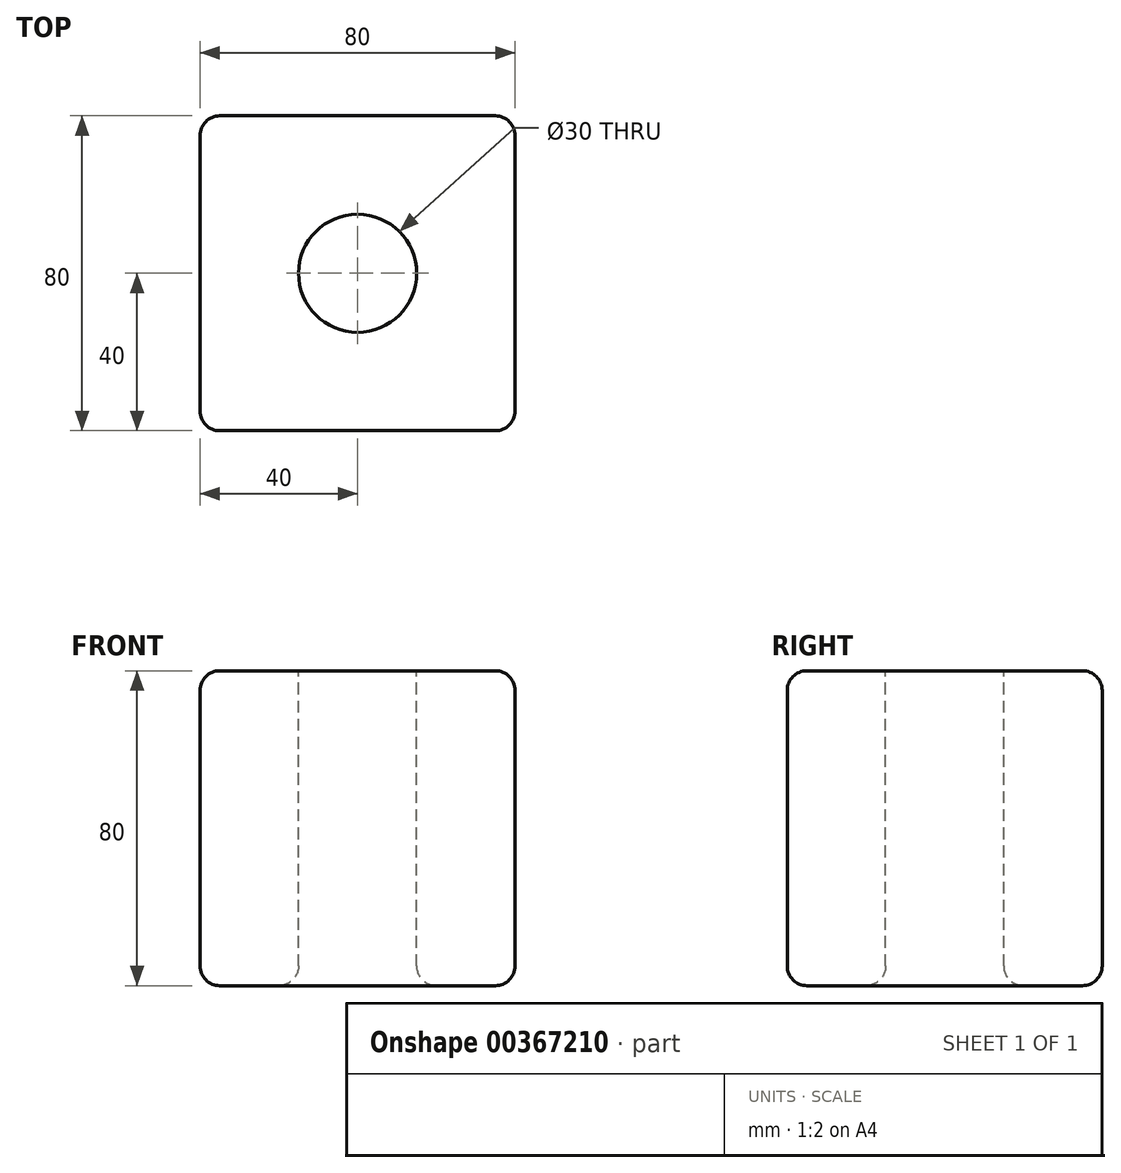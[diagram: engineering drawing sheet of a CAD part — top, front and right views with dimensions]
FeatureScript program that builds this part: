
annotation { "Feature Type Name" : "Feature", "Feature Type Description" : "" }
export const myFeature = defineFeature(function(context is Context, id is Id, definition is map)
    precondition{}
    {
        {
            var Q0;
            Q0=qCreatedBy(makeId("Top.planeOp"),FACE);
            var sketch = newSketch(context, id + "F0", { "sketchPlane" : qUnion([Q0])});
            skLineSegment(sketch, "E0.bottom", {"start": v(40, -40) * mm, "end": v(-40, -40) * mm});
            skLineSegment(sketch, "E0.top", {"start": v(40, 40) * mm, "end": v(-40, 40) * mm});
            skLineSegment(sketch, "E0.left", {"start": v(40, -40) * mm, "end": v(40, 40) * mm});
            skLineSegment(sketch, "E0.right", {"start": v(-40, -40) * mm, "end": v(-40, 40) * mm});
            skPoint(sketch, "E0.middle", {"position": v(0, 0) * mm});
            skSolve(sketch);
        }
        {
            var Q0;
            Q0=makeQuery(id+"F0.imprint","IMPRINT",FACE,{"disambiguationData":[TD([[makeQuery(id+"F0.imprint","IMPRINT",EDGE,{"derivedFrom":sQuery(id+"F0.wireOp",EDGE,"E0.bottom")}),-1.0]])]});
            extrude(context, id + "F1", {"entities" : qUnion([Q0]), "depth" : 80 * mm});
        }
        {
            var Q0;
            Q0=makeQuery(id+"F1.opExtrude","CAP_FACE",FACE,{"disambiguationData":[OSD([sQuery(id+"F0.wireOp",EDGE,"E0.bottom"),sQuery(id+"F0.wireOp",EDGE,"E0.top"),sQuery(id+"F0.wireOp",EDGE,"E0.left"),sQuery(id+"F0.wireOp",EDGE,"E0.right")])],"isStart":false});
            var sketch = newSketch(context, id + "F2", { "sketchPlane" : qUnion([Q0])});
            skCircle(sketch, "E1", {"center": v(0, 0) * mm, "radius": 15 * mm});
            skSolve(sketch);
        }
        {
            var Q0;
            Q0=makeQuery(id+"F2.imprint","IMPRINT",FACE,{"disambiguationData":[TD([[makeQuery(id+"F2.imprint","IMPRINT",EDGE,{"derivedFrom":sQuery(id+"F2.wireOp",EDGE,"E1")}),1.0]])]});
            extrude(context, id + "F3", {"entities" : qUnion([Q0]), "operationType" : NewBodyOperationType.REMOVE, "endBound" : BoundingType.THROUGH_ALL, "oppositeDirection" : true, "depth" : 25 * mm});
        }
        {
            var Q0;
            Q0=makeQuery(id+"F1.opExtrude","CAP_EDGE",EDGE,{"disambiguationData":[OSD([sQuery(id+"F0.wireOp",EDGE,"E0.top")])],"isStart":false});
            var Q1;
            Q1=makeQuery(id+"F1.opExtrude","CAP_EDGE",EDGE,{"disambiguationData":[OSD([sQuery(id+"F0.wireOp",EDGE,"E0.right")])],"isStart":false});
            var Q2;
            Q2=makeQuery(id+"F1.opExtrude","CAP_EDGE",EDGE,{"disambiguationData":[OSD([sQuery(id+"F0.wireOp",EDGE,"E0.left")])],"isStart":false});
            var Q3;
            Q3=makeQuery(id+"F1.opExtrude","CAP_EDGE",EDGE,{"disambiguationData":[OSD([sQuery(id+"F0.wireOp",EDGE,"E0.bottom")])],"isStart":false});
            var Q4;
            Q4=makeQuery(id+"F1.opExtrude","SWEPT_EDGE",EDGE,{"disambiguationData":[OSD([sQuery(id+"F0.wireOp",EDGE,"E0.bottom"),sQuery(id+"F0.wireOp",EDGE,"E0.right")])]});
            var Q5;
            Q5=makeQuery(id+"F1.opExtrude","SWEPT_FACE",FACE,{"disambiguationData":[OSD([sQuery(id+"F0.wireOp",EDGE,"E0.right")])]});
            var Q6;
            Q6=makeQuery(id+"F1.opExtrude","SWEPT_EDGE",EDGE,{"disambiguationData":[OSD([sQuery(id+"F0.wireOp",EDGE,"E0.bottom"),sQuery(id+"F0.wireOp",EDGE,"E0.left")])]});
            var Q7;
            Q7=makeQuery(id+"F1.opExtrude","SWEPT_FACE",FACE,{"disambiguationData":[OSD([sQuery(id+"F0.wireOp",EDGE,"E0.left")])]});
            var Q8;
            Q8=makeQuery(id+"F1.opExtrude","SWEPT_EDGE",EDGE,{"disambiguationData":[OSD([sQuery(id+"F0.wireOp",EDGE,"E0.top"),sQuery(id+"F0.wireOp",EDGE,"E0.left")])]});
            var Q9;
            Q9=makeQuery(id+"F1.opExtrude","CAP_EDGE",EDGE,{"disambiguationData":[OSD([sQuery(id+"F0.wireOp",EDGE,"E0.top")])],"isStart":true});
            var Q10;
            Q10=makeQuery(id+"F1.opExtrude","CAP_EDGE",EDGE,{"disambiguationData":[OSD([sQuery(id+"F0.wireOp",EDGE,"E0.bottom")])],"isStart":true});
            var Q11;
            Q11=makeQuery(id+"F3.boolean.opBoolean","COPY",EDGE,{"derivedFrom":makeQuery(id+"F3.opExtrude","CAP_EDGE",EDGE,{"disambiguationData":[OSD([sQuery(id+"F2.wireOp",EDGE,"E1")])],"isStart":true})});
            var Q12;
            Q12=makeQuery(id+"F3.boolean.opBoolean","INTERSECT",EDGE,{"derivedFrom":[makeQuery(id+"F1.opExtrude","CAP_FACE",FACE,{"disambiguationData":[OSD([sQuery(id+"F0.wireOp",EDGE,"E0.bottom"),sQuery(id+"F0.wireOp",EDGE,"E0.top"),sQuery(id+"F0.wireOp",EDGE,"E0.left"),sQuery(id+"F0.wireOp",EDGE,"E0.right")])],"isStart":true}),makeQuery(id+"F3.opExtrude","SWEPT_FACE",FACE,{"disambiguationData":[OSD([sQuery(id+"F2.wireOp",EDGE,"E1")])]})]});
            fillet(context, id + "F4", {"entities" : qUnion([Q0, Q1, Q2, Q3, Q4, Q5, Q6, Q7, Q8, Q9, Q10, Q11, Q12]), "radius" : 5 * mm, "tangentPropagation" : true, "allowEdgeOverflow" : false});
        }
    });
